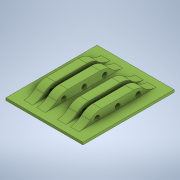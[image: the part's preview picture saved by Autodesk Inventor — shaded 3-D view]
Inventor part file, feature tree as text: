
AUTODESK INVENTOR PART (.ipt)
format: ipt  version: 2020 (Build 240168000, 168)  size: 229,376 bytes
history: native  units: mm
features: other x4, extrude x4, sketch x4, mirror x2, reference x2, chamfer x1, fillet x1
ambient origin geometry x8: Origin, YZ Plane, XZ Plane, XY Plane, X Axis, Y Axis, Z Axis, Center Point
bodies: Body1 (feature_tree)
feature tree (18):
  other  "Твердое тело1"
  extrude  "Выдавливание1"  Depth=87.5mm
  extrude  "Выдавливание2"  Depth=103.5mm
  mirror  "Зеркальное отражение1"
  extrude  "Выдавливание3"  Depth=2.8mm TaperAngle=0.0deg
  chamfer  "Фаска1"  Distance=3.0mm
  extrude  "Выдавливание4"  Depth=23.792131mm
  mirror  "Зеркальное отражение2"
  fillet  "Сопряжение1"  Radius=2.25mm
  sketch  "Эскиз1"
  sketch  "Эскиз2"
  reference  "Ссылка1"
  reference  "Ссылка2"
  sketch  "Эскиз3"
  sketch  "Эскиз4"
  other  "КВ33.000.100 - Блок переключение передач.iam"
  other  "КВ33.000.105 - Каретка:2"
  other  "КВ33.000.108 - Кулачок:2"
